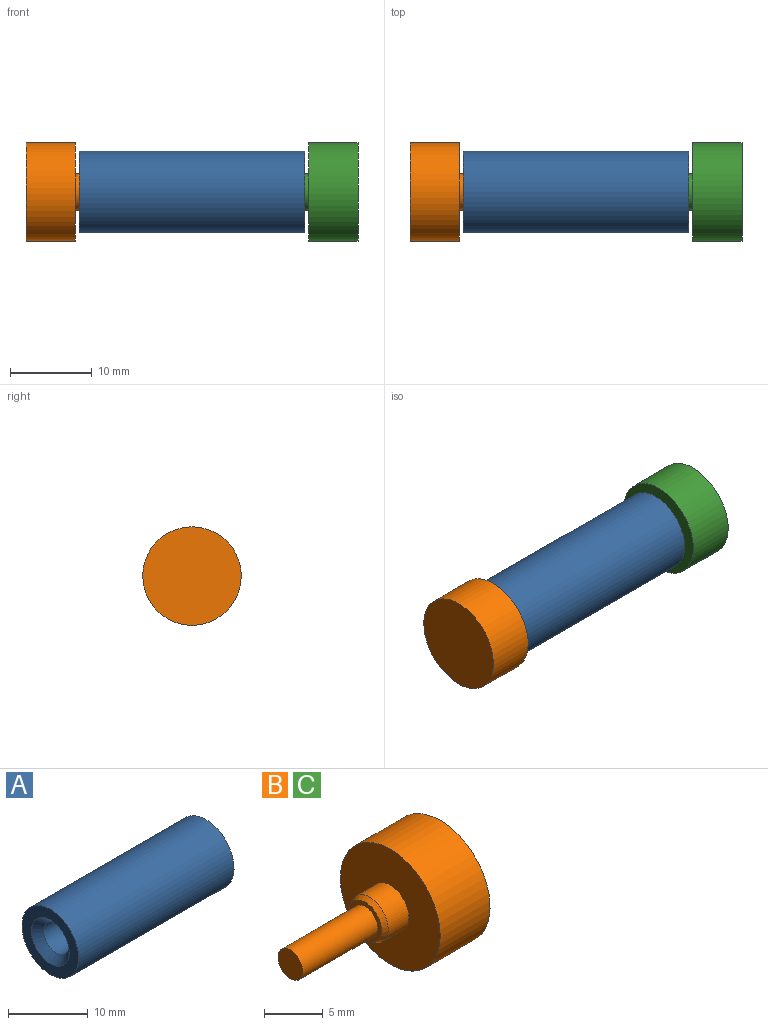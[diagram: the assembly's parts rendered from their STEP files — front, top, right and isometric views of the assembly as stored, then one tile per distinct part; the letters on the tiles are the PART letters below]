
ASSEMBLY  parts=3 mates=1
PART A: 10 faces, bbox 27.5x10x10 mm
  f0: cylinder r=1.25mm len=16.3mm, axis (1,0,0), area 128mm2, adj f6,f9
  f1: cone r=1.25mm half-angle=45deg, axis (1,0,0), area 27.7mm2, adj f4,f5
  f2: cylinder r=5mm len=27.5mm, axis (-1,0,0), area 863.9mm2, adj f3,f4
  f3: plane 10x10mm, normal (-1,0,0), area 43.1mm2, adj f2,f8
  f4: plane 10x10mm, normal (1,0,0), area 43.1mm2, adj f1,f2
  f5: cylinder r=2.25mm len=4.5mm, axis (1,0,0), area 55mm2, adj f1,f6
  f6: cone r=0mm half-angle=59deg, axis (1,0,0), area 12.8mm2, adj f0,f5
  f7: cylinder r=2.25mm len=4.5mm, axis (-1,0,0), area 55mm2, adj f8,f9
  f8: cone r=2.25mm half-angle=45deg, axis (-1,0,0), area 27.7mm2, adj f3,f7
  f9: cone r=0mm half-angle=59deg, axis (-1,0,0), area 12.8mm2, adj f0,f7
PART B: 8 faces, bbox 18x12x12 mm
  f0: plane 3x3mm, normal (-1,0,0), area 7.1mm2, adj f6
  f1: plane 12x12mm, normal (1,0,0), area 113.1mm2, adj f2
  f2: cylinder r=6mm len=12mm, axis (-1,0,0), area 226.2mm2, adj f1,f3
  f3: plane 12x12mm, normal (-1,0,0), area 97.2mm2, adj f2,f4
  f4: cylinder r=2.25mm len=4.5mm, axis (-1,0,0), area 35.3mm2, adj f3,f7
  f5: plane 3.92x3.92mm, normal (-1,0,0), area 5mm2, adj f6,f7
  f6: cylinder r=1.5mm len=9mm, axis (-1,0,0), area 84.8mm2, adj f0,f5
  f7: cone r=1.96mm half-angle=30deg, axis (1,0,0), area 7.6mm2, adj f4,f5
PART C: same geometry as B
PLACE A at identity
PLACE B rot(axis=(0,0,1),180deg) t=(-27.5,0,0)mm
PLACE C at identity
MATE fastened B.f2 <-> A.f0  axis (-1,0,0) through (-27.5,0,0)mm
